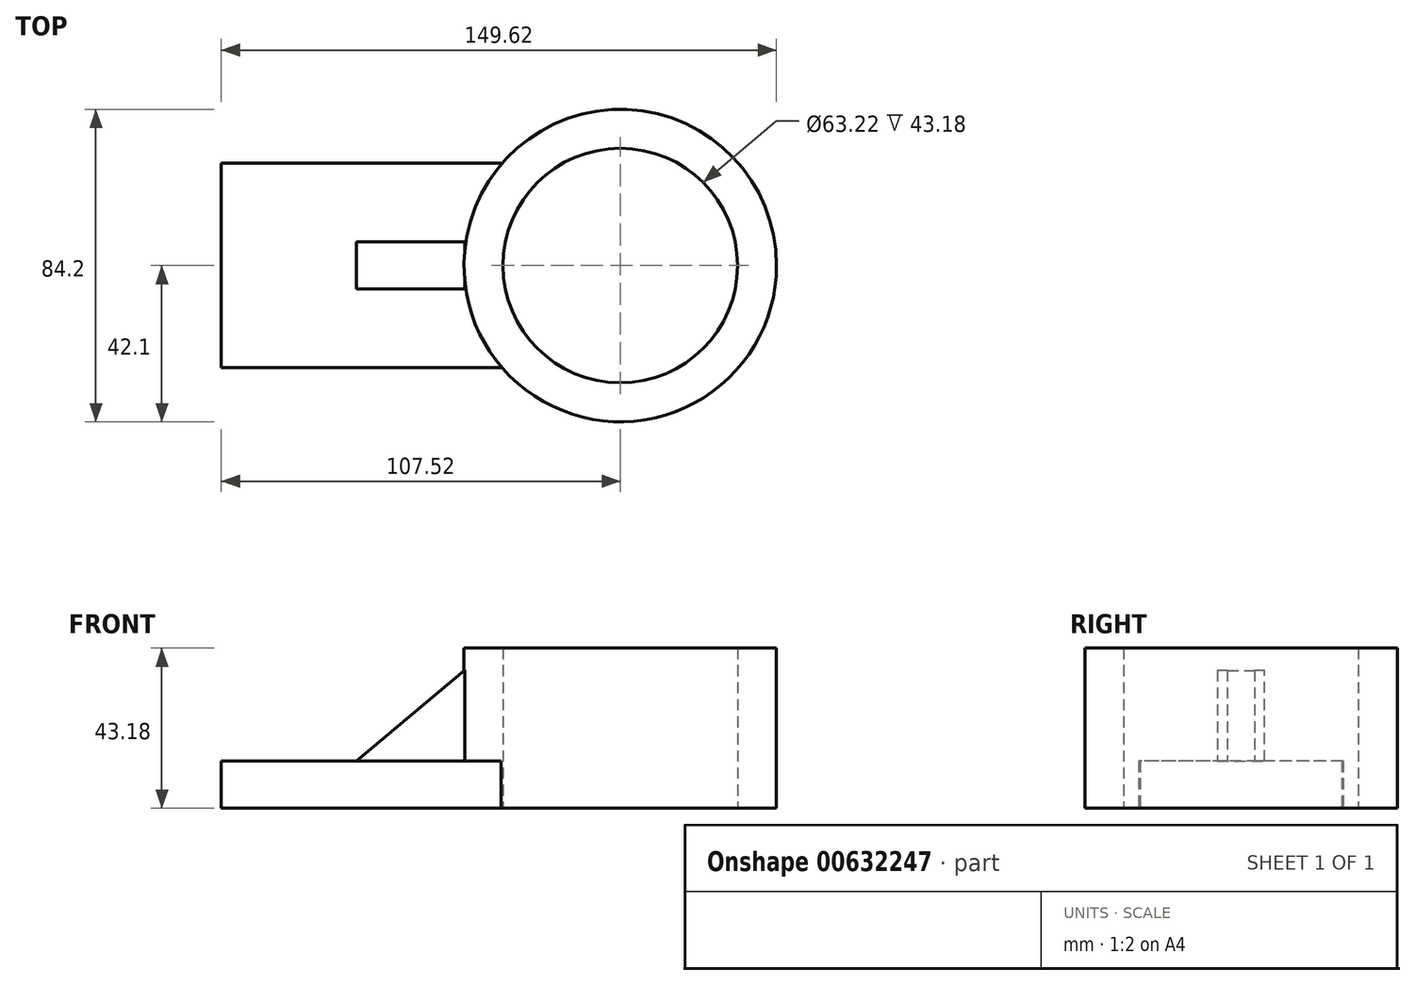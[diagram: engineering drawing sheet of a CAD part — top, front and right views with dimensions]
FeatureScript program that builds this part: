
annotation { "Feature Type Name" : "Feature", "Feature Type Description" : "" }
export const myFeature = defineFeature(function(context is Context, id is Id, definition is map)
    precondition{}
    {
        {
            var Q0;
            Q0=qCreatedBy(makeId("Top.planeOp"),FACE);
            var sketch = newSketch(context, id + "F0", { "sketchPlane" : qUnion([Q0])});
            skLineSegment(sketch, "E0.bottom", {"start": v(-107.52, 27.56) * mm, "end": v(-32.13, 27.56) * mm});
            skLineSegment(sketch, "E0.top", {"start": v(-107.52, -27.56) * mm, "end": v(-32.13, -27.56) * mm});
            skLineSegment(sketch, "E0.left", {"start": v(-107.52, 27.56) * mm, "end": v(-107.52, -27.56) * mm});
            skLineSegment(sketch, "E0.right", {"start": v(-32.13, 27.56) * mm, "end": v(-32.13, 27.2) * mm});
            skPoint(sketch, "E0.middle", {"position": v(-69.82, 0) * mm});
            skCircle(sketch, "E1", {"center": v(0, 0) * mm, "radius": 42.1 * mm});
            skCircle(sketch, "E2", {"center": v(0, 0) * mm, "radius": 31.61 * mm});
            skLineSegment(sketch, "E3.trimOffspring", {"start": v(-32.13, -27.2) * mm, "end": v(-32.13, -27.56) * mm});
            skSolve(sketch);
        }
        {
            var Q0;
            Q0=makeQuery(id+"F0.imprint","IMPRINT",FACE,{"disambiguationData":[TD([[makeQuery(id+"F0.imprint","IMPRINT",EDGE,{"derivedFrom":sQuery(id+"F0.wireOp",EDGE,"E0.bottom")}),-1.0]])]});
            extrude(context, id + "F1", {"entities" : qUnion([Q0]), "depth" : 12.7 * mm, "offsetDistance" : 25.4 * mm});
        }
        {
            var Q0;
            Q0=makeQuery(id+"F0.imprint","IMPRINT",FACE,{"disambiguationData":[TD([[makeQuery(id+"F0.imprint","IMPRINT",EDGE,{"derivedFrom":sQuery(id+"F0.wireOp",EDGE,"E2")}),-1.0]])]});
            extrude(context, id + "F2", {"entities" : qUnion([Q0]), "operationType" : NewBodyOperationType.ADD, "depth" : 43.18 * mm, "offsetDistance" : 25.4 * mm});
        }
        {
            var Q0;
            Q0=qCreatedBy(makeId("Front.planeOp"),FACE);
            var sketch = newSketch(context, id + "F3", { "sketchPlane" : qUnion([Q0])});
            skLineSegment(sketch, "E4", {"start": v(-41.94, 37.2) * mm, "end": v(-73.27, 10.92) * mm});
            skLineSegment(sketch, "E5", {"start": v(-73.27, 10.92) * mm, "end": v(-41.94, 10.92) * mm});
            skLineSegment(sketch, "E6", {"start": v(-41.94, 10.92) * mm, "end": v(-41.94, 37.2) * mm});
            skSolve(sketch);
        }
        {
            var Q0;
            Q0 = qSketchRegion(id + "F3", true);
            extrude(context, id + "F4", {"entities" : qUnion([Q0]), "operationType" : NewBodyOperationType.ADD, "endBound" : BoundingType.SYMMETRIC, "depth" : 12.7 * mm, "offsetDistance" : 25.4 * mm});
        }
    });
